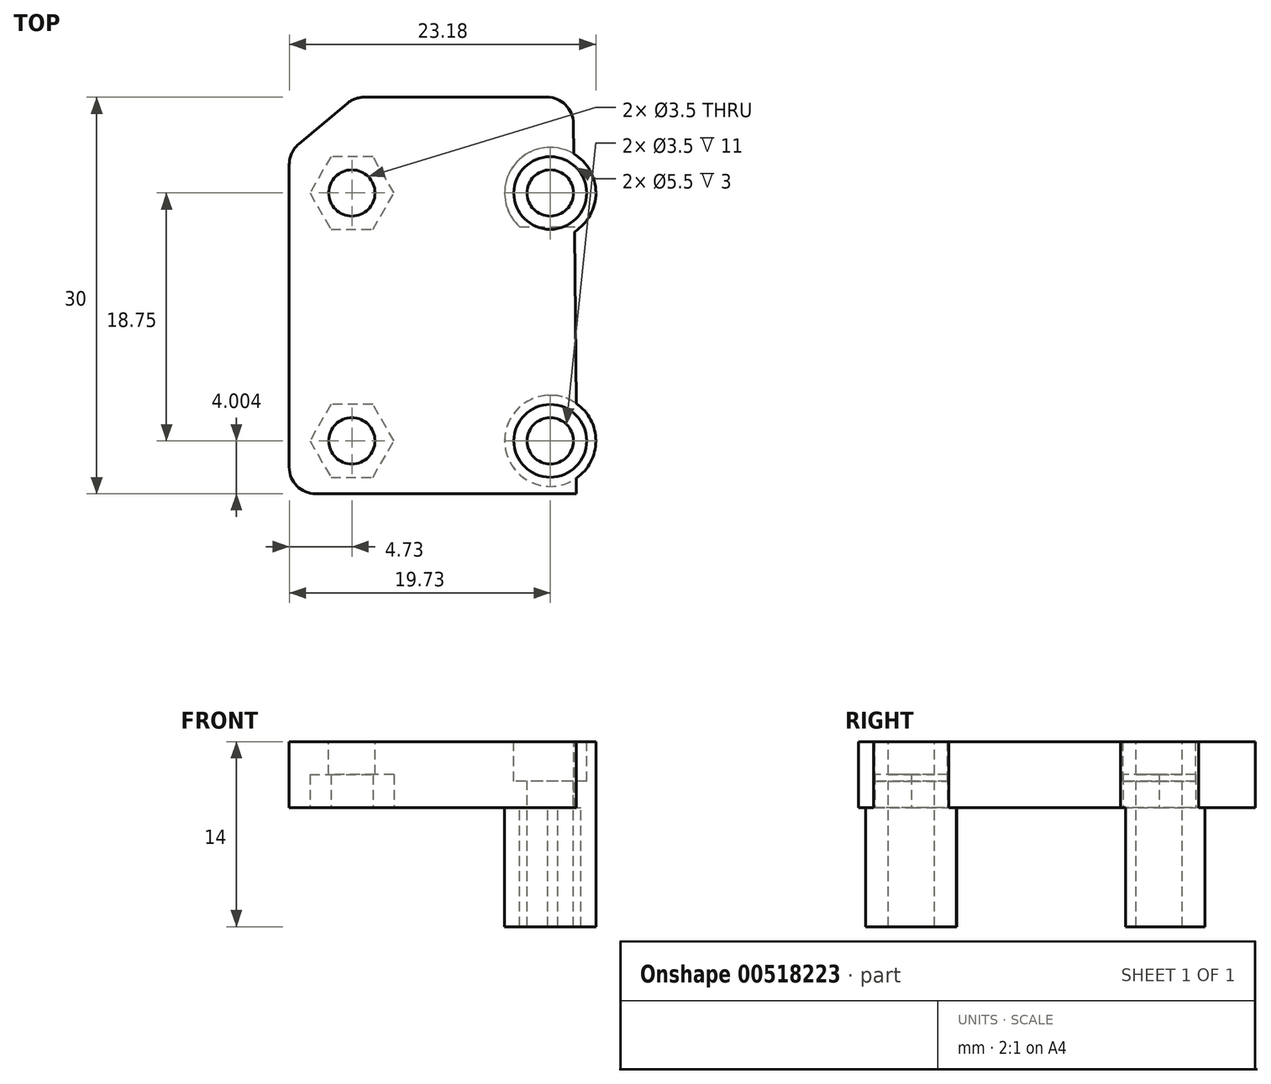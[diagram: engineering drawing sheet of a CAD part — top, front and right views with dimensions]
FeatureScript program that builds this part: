
annotation { "Feature Type Name" : "Feature", "Feature Type Description" : "" }
export const myFeature = defineFeature(function(context is Context, id is Id, definition is map)
    precondition{}
    {
        {
            var Q0;
            Q0=qCreatedBy(makeId("Top.planeOp"),FACE);
            var sketch = newSketch(context, id + "F0", { "sketchPlane" : qUnion([Q0])});
            skCircle(sketch, "E0", {"center": v(24.1, 3.87) * mm, "radius": 1.75 * mm});
            skCircle(sketch, "E1", {"center": v(24.1, -14.88) * mm, "radius": 1.75 * mm});
            skArc(sketch, "E2", {"start": v(25.93, 0.95) * mm, "mid": v(24.4, 7.31) * mm, "end": v(21.78, 1.32) * mm});
            skArc(sketch, "E3", {"start": v(23.92, -11.43) * mm, "mid": v(23.9, -18.32) * mm, "end": v(24.68, -11.47) * mm});
            skLineSegment(sketch, "E4.bottom", {"start": v(9.32, 11.12) * mm, "end": v(25.82, 11.12) * mm});
            skLineSegment(sketch, "E4.top", {"start": v(9.95, -18.88) * mm, "end": v(23.52, -18.88) * mm});
            skLineSegment(sketch, "E4.right", {"start": v(25.82, 11.12) * mm, "end": v(25.87, 6.84) * mm});
            skLineSegment(sketch, "E5.trimOffspring", {"start": v(25.93, 0.95) * mm, "end": v(26.07, -12.04) * mm});
            skLineSegment(sketch, "E6.top", {"start": v(9.88, -18.88) * mm, "end": v(4.37, -18.88) * mm});
            skLineSegment(sketch, "E6.right", {"start": v(4.37, 6.97) * mm, "end": v(4.37, -18.88) * mm});
            skCircle(sketch, "E7", {"center": v(9.1, 3.87) * mm, "radius": 1.75 * mm});
            skCircle(sketch, "E8", {"center": v(9.1, -14.88) * mm, "radius": 1.75 * mm});
            skLineSegment(sketch, "E9", {"start": v(9.32, 11.12) * mm, "end": v(4.37, 6.97) * mm});
            skLineSegment(sketch, "E10.bottom", {"start": v(21.78, 1.32) * mm, "end": v(26.42, 1.32) * mm});
            skLineSegment(sketch, "E10.top", {"start": v(23.92, -11.43) * mm, "end": v(24.69, -11.43) * mm});
            skLineSegment(sketch, "E11.bottom", {"start": v(23.52, -18.88) * mm, "end": v(26.07, -18.88) * mm});
            skLineSegment(sketch, "E11.right", {"start": v(26.07, -18.88) * mm, "end": v(26.07, -12.04) * mm});
            skLineSegment(sketch, "E12", {"start": v(24.69, -11.43) * mm, "end": v(24.68, -11.47) * mm});
            skLineSegment(sketch, "E13", {"start": v(9.95, -18.88) * mm, "end": v(9.88, -18.88) * mm});
            skSolve(sketch);
        }
        {
            var Q0;
            Q0=makeQuery(id+"F0.imprint","IMPRINT",FACE,{"disambiguationData":[TD([[makeQuery(id+"F0.imprint","IMPRINT",EDGE,{"derivedFrom":sQuery(id+"F0.wireOp",EDGE,"E0")}),-1.0]])]});
            var Q1;
            Q1=makeQuery(id+"F0.imprint","IMPRINT",FACE,{"disambiguationData":[TD([[makeQuery(id+"F0.imprint","IMPRINT",EDGE,{"derivedFrom":sQuery(id+"F0.wireOp",EDGE,"E1")}),-1.0]])]});
            var Q2;
            {var subQ0=sQuery(id+"F0.wireOp",EDGE,"E11.right");var subQ1=sQuery(id+"F0.wireOp",EDGE,"E3");var subQ3=makeQuery(id+"F0.imprint","INTERSECT",VERTEX,{"derivedFrom":[subQ1,subQ0]});Q2=makeQuery(id+"F0.imprint","IMPRINT",FACE,{"disambiguationData":[TD([[makeQuery(id+"F0.imprint","IMPRINT",EDGE,{"disambiguationData":[TD([[subQ3,-1.0]])],"derivedFrom":subQ1}),1.0]])]});}
            extrude(context, id + "F1", {"entities" : qUnion([Q0, Q1, Q2]), "oppositeDirection" : true, "depth" : 14 * mm, "offsetDistance" : 25 * mm});
        }
        {
            var Q0;
            Q0=makeQuery(id+"F0.imprint","IMPRINT",FACE,{"disambiguationData":[TD([[makeQuery(id+"F0.imprint","IMPRINT",EDGE,{"derivedFrom":sQuery(id+"F0.wireOp",EDGE,"E6.top")}),-1.0]])]});
            var Q1;
            Q1=makeQuery(id+"F0.imprint","IMPRINT",FACE,{"disambiguationData":[TD([[makeQuery(id+"F0.imprint","IMPRINT",EDGE,{"derivedFrom":sQuery(id+"F0.wireOp",EDGE,"E4.bottom")}),-1.0]])]});
            extrude(context, id + "F2", {"entities" : qUnion([Q0, Q1]), "operationType" : NewBodyOperationType.ADD, "oppositeDirection" : true, "depth" : 5 * mm, "offsetDistance" : 25 * mm});
        }
        {
            var Q0;
            Q0=makeQuery(id+"F2.opExtrude","SWEPT_EDGE",EDGE,{"disambiguationData":[OSD([sQuery(id+"F0.wireOp",EDGE,"E4.bottom"),sQuery(id+"F0.wireOp",EDGE,"E6.left"),sQuery(id+"F0.wireOp",EDGE,"E9")])]});
            var Q1;
            Q1=makeQuery(id+"F2.opExtrude","SWEPT_EDGE",EDGE,{"disambiguationData":[OSD([sQuery(id+"F0.wireOp",EDGE,"E6.right"),sQuery(id+"F0.wireOp",EDGE,"E9")])]});
            var Q2;
            Q2=makeQuery(id+"F2.opExtrude","SWEPT_EDGE",EDGE,{"disambiguationData":[OSD([sQuery(id+"F0.wireOp",EDGE,"E6.top"),sQuery(id+"F0.wireOp",EDGE,"E6.right")])]});
            var Q3;
            Q3=makeQuery(id+"F2.opExtrude","SWEPT_EDGE",EDGE,{"disambiguationData":[OSD([sQuery(id+"F0.wireOp",EDGE,"E4.bottom"),sQuery(id+"F0.wireOp",EDGE,"E4.right")])]});
            fillet(context, id + "F3", {"entities" : qUnion([Q0, Q1, Q2, Q3]), "radius" : 2 * mm, "tangentPropagation" : true, "allowEdgeOverflow" : false});
        }
        {
            var Q0;
            Q0=makeQuery(id+"F0.imprint","IMPRINT",FACE,{"disambiguationData":[TD([[makeQuery(id+"F0.imprint","IMPRINT",EDGE,{"derivedFrom":sQuery(id+"F0.wireOp",EDGE,"E4.bottom")}),-1.0]])]});
            var sketch = newSketch(context, id + "F4", { "sketchPlane" : qUnion([Q0])});
            skCircle(sketch, "E14", {"center": v(24.1, 3.87) * mm, "radius": 2.75 * mm});
            skCircle(sketch, "E15", {"center": v(24.1, -14.88) * mm, "radius": 2.75 * mm});
            skSolve(sketch);
        }
        {
            var Q0;
            {var subQ0=sQuery(id+"F4.wireOp",EDGE,"E14");var subQ1=makeQuery(id+"F0.imprint","IMPRINT",EDGE,{"derivedFrom":sQuery(id+"F0.wireOp",EDGE,"E10.bottom")});var subQ2=makeQuery(id+"F4.imprint","INTERSECT",VERTEX,{"disambiguationData":[OD(0.0)],"derivedFrom":[subQ1,subQ0]});Q0=makeQuery(id+"F4.imprint","IMPRINT",FACE,{"disambiguationData":[TD([[makeQuery(id+"F4.imprint","IMPRINT",EDGE,{"disambiguationData":[TD([[subQ2,1.0]])],"derivedFrom":subQ0}),1.0]])]});}
            var Q1;
            {var subQ0=sQuery(id+"F4.wireOp",EDGE,"E14");var subQ1=makeQuery(id+"F0.imprint","IMPRINT",EDGE,{"derivedFrom":sQuery(id+"F0.wireOp",EDGE,"E10.bottom")});var subQ2=makeQuery(id+"F4.imprint","INTERSECT",VERTEX,{"disambiguationData":[OD(0.0)],"derivedFrom":[subQ1,subQ0]});Q1=makeQuery(id+"F4.imprint","IMPRINT",FACE,{"disambiguationData":[TD([[makeQuery(id+"F4.imprint","IMPRINT",EDGE,{"disambiguationData":[TD([[subQ2,-1.0]])],"derivedFrom":subQ0}),1.0]])]});}
            var Q2;
            Q2=makeQuery(id+"F4.imprint","IMPRINT",FACE,{"disambiguationData":[TD([[makeQuery(id+"F4.imprint","IMPRINT",EDGE,{"derivedFrom":sQuery(id+"F4.wireOp",EDGE,"E15")}),1.0]])]});
            extrude(context, id + "F5", {"entities" : qUnion([Q0, Q1, Q2]), "operationType" : NewBodyOperationType.REMOVE, "oppositeDirection" : true, "depth" : 3 * mm, "offsetDistance" : 25 * mm});
        }
        {
            var Q0;
            Q0=makeQuery(id+"F2.opExtrude","CAP_FACE",FACE,{"disambiguationData":[OSD([sQuery(id+"F0.wireOp",EDGE,"E2"),sQuery(id+"F0.wireOp",EDGE,"E3"),sQuery(id+"F0.wireOp",EDGE,"E4.bottom"),sQuery(id+"F0.wireOp",EDGE,"E4.top"),sQuery(id+"F0.wireOp",EDGE,"E4.right"),sQuery(id+"F0.wireOp",EDGE,"E5.trimOffspring"),sQuery(id+"F0.wireOp",EDGE,"E6.top"),sQuery(id+"F0.wireOp",EDGE,"E6.right"),sQuery(id+"F0.wireOp",EDGE,"E7"),sQuery(id+"F0.wireOp",EDGE,"E8"),sQuery(id+"F0.wireOp",EDGE,"E9"),sQuery(id+"F0.wireOp",EDGE,"E10.bottom"),sQuery(id+"F0.wireOp",EDGE,"E10.top"),sQuery(id+"F0.wireOp",EDGE,"E11.bottom"),sQuery(id+"F0.wireOp",EDGE,"E11.right"),sQuery(id+"F0.wireOp",EDGE,"E12"),sQuery(id+"F0.wireOp",EDGE,"E13")])],"isStart":false});
            var sketch = newSketch(context, id + "F6", { "sketchPlane" : qUnion([Q0])});
            skCircle(sketch, "E16.cCircle", {"center": v(9.1, -3.87) * mm, "radius": 2.75 * mm, "construction": true});
            skLineSegment(sketch, "E16.0", {"start": v(7.51, -1.12) * mm, "end": v(10.69, -1.12) * mm});
            skLineSegment(sketch, "E16.1", {"start": v(10.69, -1.12) * mm, "end": v(12.28, -3.87) * mm});
            skLineSegment(sketch, "E16.2", {"start": v(12.28, -3.87) * mm, "end": v(10.69, -6.62) * mm});
            skLineSegment(sketch, "E16.3", {"start": v(10.69, -6.62) * mm, "end": v(7.51, -6.62) * mm});
            skLineSegment(sketch, "E16.4", {"start": v(7.51, -6.62) * mm, "end": v(5.92, -3.87) * mm});
            skLineSegment(sketch, "E16.5", {"start": v(5.92, -3.87) * mm, "end": v(7.51, -1.12) * mm});
            skPoint(sketch, "E16.0.midPoint", {"position": v(9.1, -1.12) * mm});
            skCircle(sketch, "E17.cCircle", {"center": v(9.1, 14.88) * mm, "radius": 2.75 * mm, "construction": true});
            skLineSegment(sketch, "E17.0", {"start": v(7.51, 17.63) * mm, "end": v(10.69, 17.63) * mm});
            skLineSegment(sketch, "E17.1", {"start": v(10.69, 17.63) * mm, "end": v(12.28, 14.88) * mm});
            skLineSegment(sketch, "E17.2", {"start": v(12.28, 14.88) * mm, "end": v(10.69, 12.13) * mm});
            skLineSegment(sketch, "E17.3", {"start": v(10.69, 12.13) * mm, "end": v(7.51, 12.13) * mm});
            skLineSegment(sketch, "E17.4", {"start": v(7.51, 12.13) * mm, "end": v(5.92, 14.88) * mm});
            skLineSegment(sketch, "E17.5", {"start": v(5.92, 14.88) * mm, "end": v(7.51, 17.63) * mm});
            skPoint(sketch, "E17.0.midPoint", {"position": v(9.1, 17.63) * mm});
            skSolve(sketch);
        }
        {
            var Q0;
            Q0=makeQuery(id+"F6.imprint","IMPRINT",FACE,{"disambiguationData":[TD([[makeQuery(id+"F6.imprint","IMPRINT",EDGE,{"derivedFrom":sQuery(id+"F6.wireOp",EDGE,"E16.0")}),-1.0]])]});
            var Q1;
            Q1=makeQuery(id+"F6.imprint","IMPRINT",FACE,{"disambiguationData":[TD([[makeQuery(id+"F6.imprint","IMPRINT",EDGE,{"derivedFrom":sQuery(id+"F6.wireOp",EDGE,"E17.0")}),-1.0]])]});
            extrude(context, id + "F7", {"entities" : qUnion([Q0, Q1]), "operationType" : NewBodyOperationType.REMOVE, "oppositeDirection" : true, "depth" : 2.5 * mm, "offsetDistance" : 25 * mm});
        }
    });
